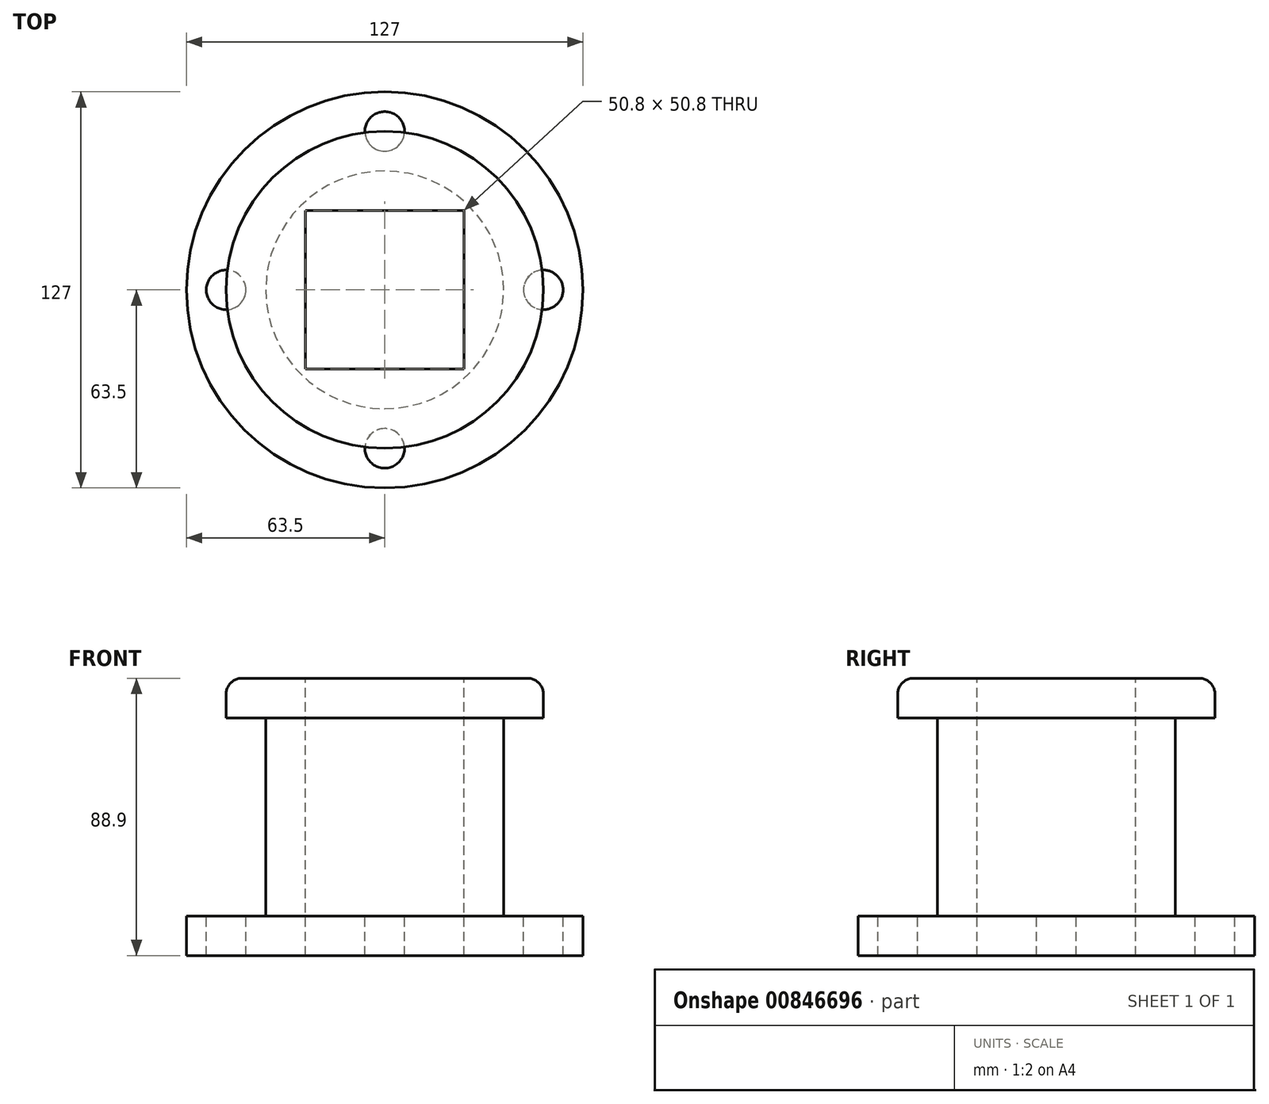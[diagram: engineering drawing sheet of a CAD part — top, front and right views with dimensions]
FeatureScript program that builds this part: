
annotation { "Feature Type Name" : "Feature", "Feature Type Description" : "" }
export const myFeature = defineFeature(function(context is Context, id is Id, definition is map)
    precondition{}
    {
        {
            var Q0;
            Q0=qCreatedBy(makeId("Top.planeOp"),FACE);
            var sketch = newSketch(context, id + "F0", { "sketchPlane" : qUnion([Q0])});
            skCircle(sketch, "E0", {"center": v(0, 0) * mm, "radius": 38.1 * mm});
            skSolve(sketch);
        }
        {
            var Q0;
            Q0 = qSketchRegion(id + "F0", true);
            extrude(context, id + "F1", {"entities" : qUnion([Q0]), "depth" : 63.5 * mm, "offsetDistance" : 25.4 * mm});
        }
        {
            var Q0;
            Q0=qCreatedBy(makeId("Top.planeOp"),FACE);
            var sketch = newSketch(context, id + "F2", { "sketchPlane" : qUnion([Q0])});
            skCircle(sketch, "E1", {"center": v(0, 0) * mm, "radius": 63.5 * mm});
            skSolve(sketch);
        }
        {
            var Q0;
            Q0 = qSketchRegion(id + "F2", true);
            extrude(context, id + "F3", {"entities" : qUnion([Q0]), "operationType" : NewBodyOperationType.ADD, "oppositeDirection" : true, "depth" : 12.7 * mm, "offsetDistance" : 25.4 * mm});
        }
        {
            var Q0;
            Q0=makeQuery(id+"F3.opExtrude","CAP_FACE",FACE,{"disambiguationData":[OSD([sQuery(id+"F2.wireOp",EDGE,"E1")])],"isStart":true});
            var sketch = newSketch(context, id + "F4", { "sketchPlane" : qUnion([Q0])});
            skCircle(sketch, "E2", {"center": v(-50.8, 0) * mm, "radius": 6.35 * mm});
            skCircle(sketch, "E3", {"center": v(0, 50.8) * mm, "radius": 6.35 * mm});
            skCircle(sketch, "E4", {"center": v(50.8, 0) * mm, "radius": 6.35 * mm});
            skCircle(sketch, "E5", {"center": v(0, -50.8) * mm, "radius": 6.35 * mm});
            skSolve(sketch);
        }
        {
            var Q0;
            Q0 = qSketchRegion(id + "F4", true);
            extrude(context, id + "F5", {"entities" : qUnion([Q0]), "operationType" : NewBodyOperationType.REMOVE, "oppositeDirection" : true, "depth" : 25.4 * mm, "offsetDistance" : 25.4 * mm});
        }
        {
            var Q0;
            Q0=makeQuery(id+"F1.opExtrude","CAP_FACE",FACE,{"disambiguationData":[OSD([sQuery(id+"F0.wireOp",EDGE,"E0")])],"isStart":false});
            var sketch = newSketch(context, id + "F6", { "sketchPlane" : qUnion([Q0])});
            skCircle(sketch, "E6", {"center": v(0, 0) * mm, "radius": 50.8 * mm});
            skSolve(sketch);
        }
        {
            var Q0;
            Q0 = qSketchRegion(id + "F6", true);
            extrude(context, id + "F7", {"entities" : qUnion([Q0]), "operationType" : NewBodyOperationType.ADD, "depth" : 12.7 * mm, "offsetDistance" : 25.4 * mm});
        }
        {
            var Q0;
            Q0=makeQuery(id+"F7.opExtrude","CAP_EDGE",EDGE,{"disambiguationData":[OSD([sQuery(id+"F6.wireOp",EDGE,"E6")])],"isStart":false});
            fillet(context, id + "F8", {"entities" : qUnion([Q0]), "radius" : 5.08 * mm, "tangentPropagation" : true, "allowEdgeOverflow" : false});
        }
        {
            var Q0;
            Q0=makeQuery(id+"F7.opExtrude","CAP_FACE",FACE,{"disambiguationData":[OSD([sQuery(id+"F6.wireOp",EDGE,"E6")])],"isStart":false});
            var sketch = newSketch(context, id + "F9", { "sketchPlane" : qUnion([Q0])});
            skLineSegment(sketch, "E7.bottom", {"start": v(25.4, -25.4) * mm, "end": v(-25.4, -25.4) * mm});
            skLineSegment(sketch, "E7.top", {"start": v(25.4, 25.4) * mm, "end": v(-25.4, 25.4) * mm});
            skLineSegment(sketch, "E7.left", {"start": v(25.4, -25.4) * mm, "end": v(25.4, 25.4) * mm});
            skLineSegment(sketch, "E7.right", {"start": v(-25.4, -25.4) * mm, "end": v(-25.4, 25.4) * mm});
            skSolve(sketch);
        }
        {
            var Q0;
            Q0 = qSketchRegion(id + "F9", true);
            extrude(context, id + "F10", {"entities" : qUnion([Q0]), "operationType" : NewBodyOperationType.REMOVE, "oppositeDirection" : true, "depth" : 132.84 * mm, "offsetDistance" : 25.4 * mm});
        }
    });
